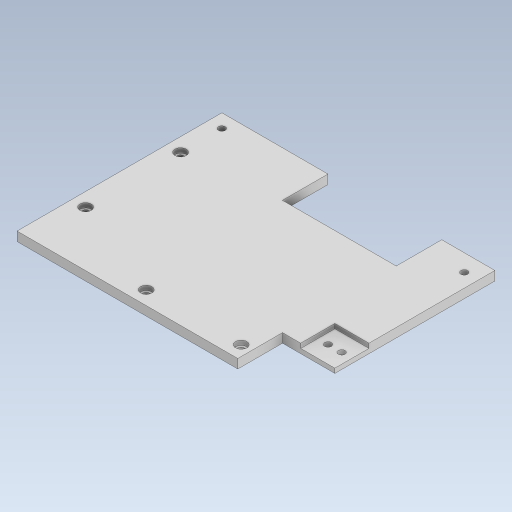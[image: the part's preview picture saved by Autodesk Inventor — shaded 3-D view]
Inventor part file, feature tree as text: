
AUTODESK INVENTOR PART (.ipt)
format: ipt  version: 2023.5 (Build 275446000, 446)  size: 152,064 bytes
history: native  units: in
note: dims shown in document units (in); Inventor stores cm internally (conversion verified against a paired STEP export)
features: extrude x2, sketch x1
ambient origin geometry x8: Origin, YZ Plane, XZ Plane, XY Plane, X Axis, Y Axis, Z Axis, Center Point
bodies: Solid1 (feature_tree)
feature tree (3):
  sketch  "Sketch1"  dims[d0=0.1575in d1=0.0in d2=0.0787in d3=0.0in d4=0.4724in d5=0.2953in d6=0.4724in d7=0.3543in d8=0.0in d10=0.0in d11=0.315in]
  extrude  "Extrusion1"  Depth=0.0787in TaperAngle=0.0deg
  extrude  "Extrusion2"  Depth=0.315in
